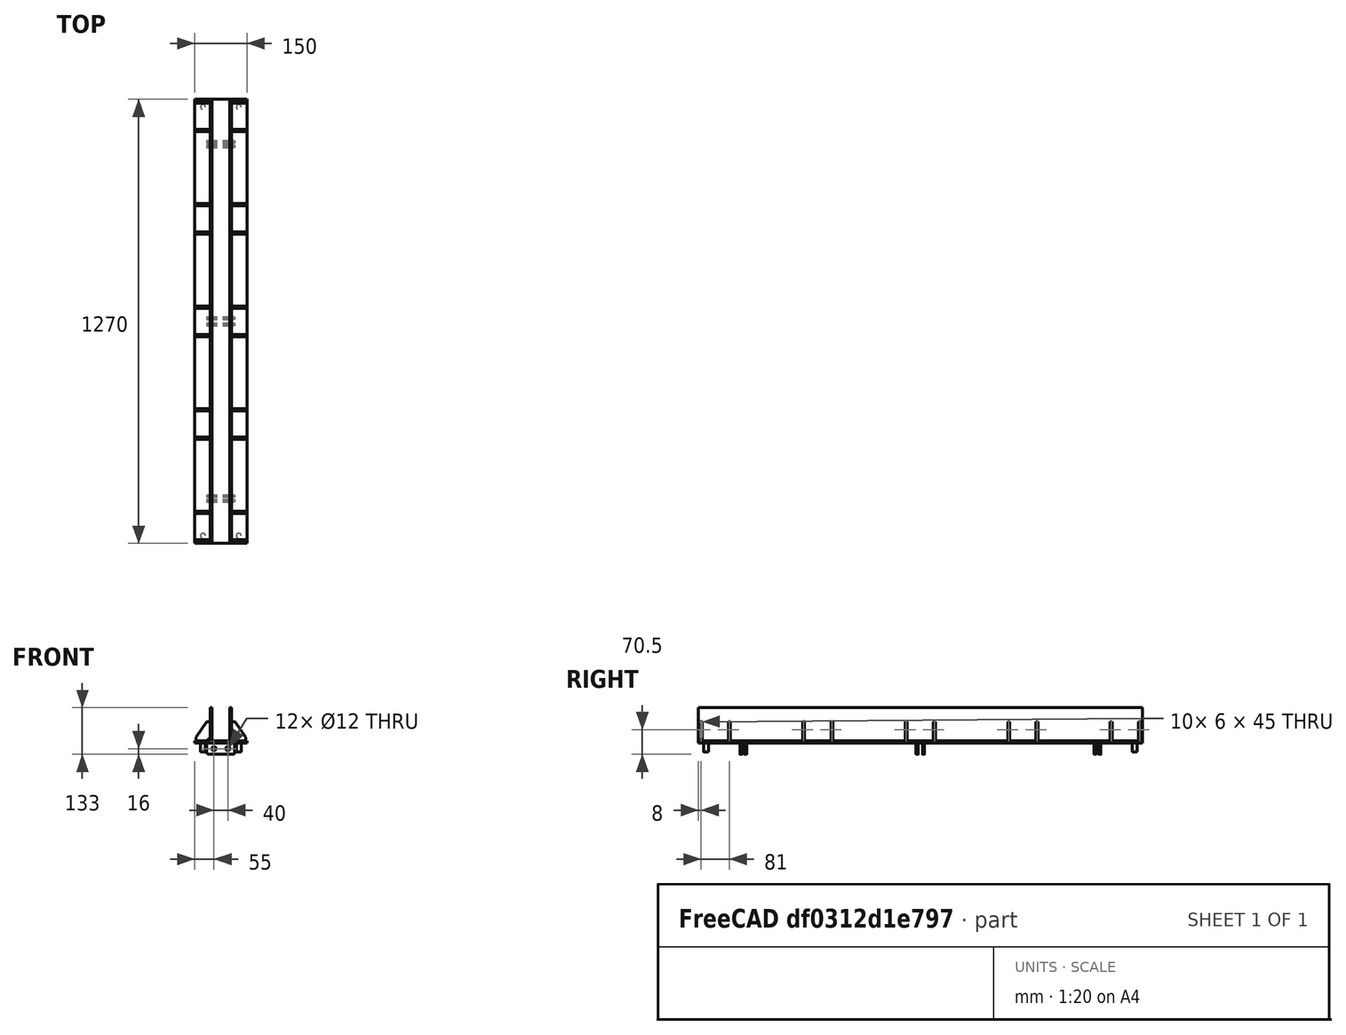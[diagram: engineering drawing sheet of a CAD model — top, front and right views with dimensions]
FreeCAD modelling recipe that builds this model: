
FCSTD DOCUMENT  (FreeCAD 0.21R33771 (Git))
Label: Transom 1270_95_10kN_half
License: All rights reserved
LicenseURL: https://en.wikipedia.org/wiki/All_rights_reserved
objects: Part::FeaturePython×12, Sketcher::SketchObject×3, Fem::ConstraintDisplacement×2, PartDesign::Pad×1, PartDesign::Body×1, Part::Cylinder×1, Part::Compound×1, App::MaterialObjectPython×1, Fem::FemSolverObjectPython×1, Part::MultiFuse×1, Fem::ConstraintForce×1, Fem::FemMeshObjectPython×1, Fem::FemAnalysis×1
note: 19 computed .brp shape members not serialized (recipe doc carries the construction recipe); baked Part::Feature solids carry a one-line shape summary decoded from their .brp

FEATURE [Sketcher::SketchObject] Sketch
  FullyConstrained = true
  MapMode = 5
  Placement = pos=(0,0,0) rot=(1,0,0;1.5708rad)
  sketch-geometry (14):
    g0: LineSegment StartX=0 StartY=0 StartZ=0 EndX=75 EndY=0 EndZ=0
    g1: LineSegment StartX=75 StartY=0 StartZ=0 EndX=75 EndY=6 EndZ=0
    g2: LineSegment StartX=75 StartY=6 StartZ=0 EndX=31 EndY=6 EndZ=0
    g3: LineSegment StartX=31 StartY=6 StartZ=0 EndX=31 EndY=101 EndZ=0
    g4: LineSegment StartX=31 StartY=101 StartZ=0 EndX=25 EndY=101 EndZ=0
    g5: LineSegment StartX=25 StartY=101 StartZ=0 EndX=25 EndY=6 EndZ=0
    g6: LineSegment StartX=25 StartY=6 StartZ=0 EndX=0 EndY=6 EndZ=0
    g7: LineSegment StartX=0 StartY=6 StartZ=0 EndX=-25 EndY=6 EndZ=0
    g8: LineSegment StartX=-25 StartY=6 StartZ=0 EndX=-25 EndY=101 EndZ=0
    g9: LineSegment StartX=-25 StartY=101 StartZ=0 EndX=-31 EndY=101 EndZ=0
    g10: LineSegment StartX=-31 StartY=101 StartZ=0 EndX=-31 EndY=6 EndZ=0
    g11: LineSegment StartX=-31 StartY=6 StartZ=0 EndX=-75 EndY=6 EndZ=0
    g12: LineSegment StartX=-75 StartY=6 StartZ=0 EndX=-75 EndY=0 EndZ=0
    g13: LineSegment StartX=-75 StartY=0 StartZ=0 EndX=0 EndY=0 EndZ=0
  constraints (41):
    c: Coincident(g-1,g0)
    c: PointOnObject(g0,g-1)
    c: Coincident(g0,g1)
    c: Coincident(g1,g2)
    c: Horizontal(g2)
    c: Coincident(g2,g3)
    c: Vertical(g3)
    c: Coincident(g3,g4)
    c: Horizontal(g4)
    c: Coincident(g4,g5)
    c: Vertical(g5)
    c: Coincident(g5,g6)
    c: PointOnObject(g6,g-2)
    c: Horizontal(g6)
    c: DistanceX(g4,g4) = 6
    c: Vertical(g1)
    c: DistanceY(g1,g1) = 6
    c: DistanceY(g0,g6) = 6
    c: DistanceX(g6,g5) = 25
    c: DistanceX(g0,g0) = 75
    c: DistanceY(g3,g3) = 95
    c: Coincident(g6,g7)
    c: Coincident(g7,g8)
    c: Vertical(g8)
    c: Coincident(g8,g9)
    c: Horizontal(g9)
    c: Coincident(g9,g10)
    c: Vertical(g10)
    c: Coincident(g10,g11)
    c: Horizontal(g11)
    c: Coincident(g11,g12)
    c: Coincident(g12,g13)
    c: Coincident(g13,g-1)
    c: Horizontal(g13)
    c: Equal(g5,g10)
    c: Horizontal(g4,g8)
    c: Horizontal(g5,g7)
    c: Vertical(g12)
    c: Equal(g6,g7)
    c: Equal(g2,g11)
    c: Equal(g4,g9)
FEATURE [PartDesign::Pad] Pad
  Direction = (0,-1,2e-16)
  Length = 1270
  Length2 = 10
  Placement = pos=(0,0,0) rot=(1,0,0;1.5708rad)
  Profile = -> Sketch
  ReferenceAxis = -> Sketch [N_Axis]
  Refine = true
  Type = 0
FEATURE [PartDesign::Body] Body
  Group = -> [Sketch,Pad]
  Origin = -> Origin
  Placement = pos=(0,0,0) rot=(0,0,1;3.14159rad)
  Tip = -> Pad
FEATURE [Part::Cylinder] Cylinder
  Angle = 360
  AttacherType = Attacher::AttachEngine3D
  FirstAngle = 0
  Height = 25
  Placement = pos=(51,22,0) rot=(1,0,0;3.14159rad)
  Radius = 7
  SecondAngle = 0
FEATURE [Part::FeaturePython] Array  label="Array_ Transom to Jack Pin"  # Draft array (typed FeaturePython)
  AlwaysSyncPlacement = false
  Angle = 360
  ArrayType = 0
  Axis = (0,0,1)
  Base = -> Cylinder
  Center = (0,0,0)
  Count = 4
  ExpandArray = false
  Fuse = false
  IntervalAxis = (0,0,0)
  IntervalX = (-102,0,0)
  IntervalY = (0,1226,0)
  IntervalZ = (0,0,100)
  NumberCircles = 3
  NumberPolar = 5
  NumberX = 2
  NumberY = 2
  NumberZ = 1
  PlacementList = 4 placements: [(51,22,0),(51,1248,0),(-51,22,0),(-51,1248,0)]
  RadialDistance = 50
  ScaleList = (4) [(1,1,1),(1,1,1),(1,1,1),(1,1,1)]
  Symmetry = 1
  TangentialDistance = 25
FEATURE [Part::FeaturePython] b_Transom_Web_001_  label="Transom Web_Body_001"  # a2plus imported part (geometry in sourceFile) (typed FeaturePython)
  Placement = pos=(31,11,6) rot=(0,0,1;0rad)
  a2p_Version = 0.4.68
  fixedPosition = true
  objectType = a2pPart
  sourceFile = ./Transom Web.FCStd
  sourcePart = Body
  subassemblyImport = false
  timeLastImport = 1.75005e+09
  updateColors = true
FEATURE [Part::FeaturePython] b_Transom_Cleat_001_  label="Transom Cleat_001"  # a2plus imported part (geometry in sourceFile) (typed FeaturePython)
  Placement = pos=(0,125,0) rot=(0,0,1;0rad)
  a2p_Version = 0.4.68
  fixedPosition = true
  objectType = a2pPart
  sourceFile = ./Transom Cleat.FCStd
  subassemblyImport = false
  timeLastImport = 1.75161e+09
  updateColors = true
FEATURE [Part::FeaturePython] b_Transom_Cleat_001_001  label="Transom Cleat_002"  # a2plus imported part (geometry in sourceFile) (typed FeaturePython)
  Placement = pos=(0,138,0) rot=(0,0,1;0rad)
  a2p_Version = 0.4.68
  fixedPosition = false
  objectType = a2pPart
  sourceFile = ./Transom Cleat.FCStd
  subassemblyImport = false
  timeLastImport = 1.75161e+09
  updateColors = true
FEATURE [Part::FeaturePython] b_Transom_Cleat_001_002  label="Transom Cleat_003"  # a2plus imported part (geometry in sourceFile) (typed FeaturePython)
  Placement = pos=(0,1138,0) rot=(0,0,1;0rad)
  a2p_Version = 0.4.68
  fixedPosition = false
  objectType = a2pPart
  sourceFile = ./Transom Cleat.FCStd
  subassemblyImport = false
  timeLastImport = 1.75161e+09
  updateColors = true
FEATURE [Part::FeaturePython] b_Transom_Cleat_001_003  label="Transom Cleat_004"  # a2plus imported part (geometry in sourceFile) (typed FeaturePython)
  Placement = pos=(0,1151,0) rot=(0,0,1;0rad)
  a2p_Version = 0.4.68
  fixedPosition = false
  objectType = a2pPart
  sourceFile = ./Transom Cleat.FCStd
  subassemblyImport = false
  timeLastImport = 1.75161e+09
  updateColors = true
FEATURE [Sketcher::SketchObject] Sketch001
  FullyConstrained = true
  Placement = pos=(0,0,6) rot=(0,0,1;0rad)
  sketch-geometry (40):
    g0: LineSegment StartX=31 StartY=81 StartZ=0 EndX=31 EndY=16 EndZ=0
    g1: LineSegment StartX=31 StartY=16 StartZ=0 EndX=81 EndY=16 EndZ=0
    g2: LineSegment StartX=81 StartY=16 StartZ=0 EndX=81 EndY=81 EndZ=0
    g3: LineSegment StartX=81 StartY=81 StartZ=0 EndX=31 EndY=81 EndZ=0
    g4: LineSegment StartX=31 StartY=667.5 StartZ=0 EndX=31 EndY=602.5 EndZ=0
    g5: LineSegment StartX=31 StartY=602.5 StartZ=0 EndX=81 EndY=602.5 EndZ=0
    g6: LineSegment StartX=81 StartY=602.5 StartZ=0 EndX=81 EndY=667.5 EndZ=0
    g7: LineSegment StartX=81 StartY=667.5 StartZ=0 EndX=31 EndY=667.5 EndZ=0
    g8: LineSegment StartX=31 StartY=1189 StartZ=0 EndX=31 EndY=1254 EndZ=0
    g9: LineSegment StartX=31 StartY=1254 StartZ=0 EndX=81 EndY=1254 EndZ=0
    g10: LineSegment StartX=81 StartY=1254 StartZ=0 EndX=81 EndY=1189 EndZ=0
    g11: LineSegment StartX=81 StartY=1189 StartZ=0 EndX=31 EndY=1189 EndZ=0
    g12: LineSegment StartX=31 StartY=374.25 StartZ=0 EndX=31 EndY=309.25 EndZ=0
    g13: LineSegment StartX=31 StartY=309.25 StartZ=0 EndX=81 EndY=309.25 EndZ=0
    g14: LineSegment StartX=81 StartY=309.25 StartZ=0 EndX=81 EndY=374.25 EndZ=0
    g15: LineSegment StartX=81 StartY=374.25 StartZ=0 EndX=31 EndY=374.25 EndZ=0
    g16: LineSegment StartX=31 StartY=960.75 StartZ=0 EndX=31 EndY=895.75 EndZ=0
    g17: LineSegment StartX=31 StartY=895.75 StartZ=0 EndX=81 EndY=895.75 EndZ=0
    g18: LineSegment StartX=81 StartY=895.75 StartZ=0 EndX=81 EndY=960.75 EndZ=0
    g19: LineSegment StartX=81 StartY=960.75 StartZ=0 EndX=31 EndY=960.75 EndZ=0
    g20: LineSegment StartX=-31 StartY=81 StartZ=0 EndX=-31 EndY=16 EndZ=0
    g21: LineSegment StartX=-31 StartY=16 StartZ=0 EndX=-81 EndY=16 EndZ=0
    g22: LineSegment StartX=-81 StartY=16 StartZ=0 EndX=-81 EndY=81 EndZ=0
    g23: LineSegment StartX=-81 StartY=81 StartZ=0 EndX=-31 EndY=81 EndZ=0
    g24: LineSegment StartX=-31 StartY=667.5 StartZ=0 EndX=-31 EndY=602.5 EndZ=0
    g25: LineSegment StartX=-31 StartY=602.5 StartZ=0 EndX=-81 EndY=602.5 EndZ=0
    g26: LineSegment StartX=-81 StartY=602.5 StartZ=0 EndX=-81 EndY=667.5 EndZ=0
    g27: LineSegment StartX=-81 StartY=667.5 StartZ=0 EndX=-31 EndY=667.5 EndZ=0
    g28: LineSegment StartX=-31 StartY=1189 StartZ=0 EndX=-31 EndY=1254 EndZ=0
    g29: LineSegment StartX=-31 StartY=1254 StartZ=0 EndX=-81 EndY=1254 EndZ=0
    g30: LineSegment StartX=-81 StartY=1254 StartZ=0 EndX=-81 EndY=1189 EndZ=0
    g31: LineSegment StartX=-81 StartY=1189 StartZ=0 EndX=-31 EndY=1189 EndZ=0
    g32: LineSegment StartX=-31 StartY=374.25 StartZ=0 EndX=-31 EndY=309.25 EndZ=0
    g33: LineSegment StartX=-31 StartY=309.25 StartZ=0 EndX=-81 EndY=309.25 EndZ=0
    g34: LineSegment StartX=-81 StartY=309.25 StartZ=0 EndX=-81 EndY=374.25 EndZ=0
    g35: LineSegment StartX=-81 StartY=374.25 StartZ=0 EndX=-31 EndY=374.25 EndZ=0
    g36: LineSegment StartX=-31 StartY=960.75 StartZ=0 EndX=-31 EndY=895.75 EndZ=0
    g37: LineSegment StartX=-31 StartY=895.75 StartZ=0 EndX=-81 EndY=895.75 EndZ=0
    g38: LineSegment StartX=-81 StartY=895.75 StartZ=0 EndX=-81 EndY=960.75 EndZ=0
    g39: LineSegment StartX=-81 StartY=960.75 StartZ=0 EndX=-31 EndY=960.75 EndZ=0
  constraints (120):
    c: Coincident(g0,g1)
    c: Coincident(g1,g2)
    c: Coincident(g2,g3)
    c: Coincident(g3,g0)
    c: Vertical(g0)
    c: Vertical(g2)
    c: Horizontal(g1)
    c: Horizontal(g3)
    c: DistanceY(g2,g2) = 65
    c: DistanceX(g3,g3) = 50
    c: DistanceY(g-1,g0) = 16
    c: DistanceX(g-1,g0) = 31
    c: Coincident(g4,g5)
    c: Coincident(g5,g6)
    c: Coincident(g6,g7)
    c: Coincident(g7,g4)
    c: Vertical(g4)
    c: Vertical(g6)
    c: Horizontal(g5)
    c: Horizontal(g7)
    c: Coincident(g8,g9)
    c: Coincident(g9,g10)
    c: Coincident(g10,g11)
    c: Coincident(g11,g8)
    c: Vertical(g8)
    c: Vertical(g10)
    c: Horizontal(g9)
    c: Horizontal(g11)
    c: Equal(g2,g6)
    c: Equal(g6,g10)
    c: Equal(g1,g5)
    c: Equal(g5,g9)
    c: Vertical(g2,g6)
    c: Vertical(g6,g10)
    c: DistanceY(g2,g5) = 521.5
    c: DistanceY(g6,g9) = 586.5
    c: Coincident(g12,g13)
    c: Coincident(g13,g14)
    c: Coincident(g14,g15)
    c: Coincident(g15,g12)
    c: Vertical(g12)
    c: Vertical(g14)
    c: Horizontal(g13)
    c: Horizontal(g15)
    c: Coincident(g16,g17)
    c: Coincident(g17,g18)
    c: Coincident(g18,g19)
    c: Coincident(g19,g16)
    c: Vertical(g16)
    c: Vertical(g18)
    c: Horizontal(g17)
    c: Horizontal(g19)
    c: Vertical(g0,g12)
    c: Vertical(g12,g16)
    c: Vertical(g2,g13)
    c: Vertical(g13,g17)
    c: Equal(g0,g12)
    c: Equal(g12,g16)
    c: DistanceY(g2,g13) = 228.25
    c: DistanceY(g6,g17) = 228.25
    c: Coincident(g20,g21)
    c: Coincident(g21,g22)
    c: Coincident(g22,g23)
    c: Coincident(g23,g20)
    c: Vertical(g20)
    c: Vertical(g22)
    c: Horizontal(g21)
    c: Horizontal(g23)
    c: Coincident(g24,g25)
    c: Coincident(g25,g26)
    c: Coincident(g26,g27)
    c: Coincident(g27,g24)
    c: Vertical(g24)
    c: Vertical(g26)
    c: Horizontal(g25)
    c: Horizontal(g27)
    c: Coincident(g28,g29)
    c: Coincident(g29,g30)
    c: Coincident(g30,g31)
    c: Coincident(g31,g28)
    c: Vertical(g28)
    c: Vertical(g30)
    c: Horizontal(g29)
    c: Horizontal(g31)
    c: Equal(g22,g26)
    c: Equal(g26,g30)
    c: Equal(g21,g25)
    c: Equal(g25,g29)
    c: Coincident(g32,g33)
    c: Coincident(g33,g34)
    c: Coincident(g34,g35)
    c: Coincident(g35,g32)
    c: Vertical(g32)
    c: Vertical(g34)
    c: Horizontal(g33)
    c: Horizontal(g35)
    c: Coincident(g36,g37)
    c: Coincident(g37,g38)
    c: Coincident(g38,g39)
    c: Coincident(g39,g36)
    c: Vertical(g36)
    c: Vertical(g38)
    c: Horizontal(g37)
    c: Horizontal(g39)
    c: Equal(g20,g32)
    c: Equal(g32,g36)
    c: Horizontal(g32,g12)
    c: Horizontal(g24,g4)
    c: Horizontal(g36,g16)
    c: Horizontal(g28,g8)
    c: Vertical(g21,g33)
    c: Vertical(g33,g25)
    c: Vertical(g25,g37)
    c: Vertical(g37,g30)
    c: Equal(g0,g22)
    c: DistanceY(g-1,g20) = 16
    c: DistanceX(g20,g-1) = 31
    c: Equal(g3,g23)
    c: Equal(g15,g35)
    c: Equal(g19,g39)
FEATURE [Part::FeaturePython] b_Transom_Cleat_001_004  label="Transom Cleat_005"  # a2plus imported part (geometry in sourceFile) (typed FeaturePython)
  Placement = pos=(0,647,0) rot=(0,0,1;0rad)
  a2p_Version = 0.4.68
  fixedPosition = false
  objectType = a2pPart
  sourceFile = ./Transom Cleat.FCStd
  subassemblyImport = false
  timeLastImport = 1.75161e+09
  updateColors = true
FEATURE [Part::FeaturePython] b_Transom_Cleat_001_005  label="Transom Cleat_006"  # a2plus imported part (geometry in sourceFile) (typed FeaturePython)
  Placement = pos=(-4.61864e-06,629,3.05661e-08) rot=(0,0,1;0rad)
  a2p_Version = 0.4.68
  fixedPosition = false
  objectType = a2pPart
  sourceFile = ./Transom Cleat.FCStd
  subassemblyImport = false
  timeLastImport = 1.75161e+09
  updateColors = true
FEATURE [Sketcher::SketchObject] Sketch002
  FullyConstrained = true
  MapMode = 5
  Placement = pos=(0,0,1e-15) rot=(1,0,0;3.14159rad)
  sketch-geometry (12):
    g0: LineSegment StartX=-80 StartY=-55 StartZ=0 EndX=-80 EndY=-75 EndZ=0
    g1: LineSegment StartX=-80 StartY=-75 StartZ=0 EndX=80 EndY=-75 EndZ=0
    g2: LineSegment StartX=80 StartY=-75 StartZ=0 EndX=80 EndY=-55 EndZ=0
    g3: LineSegment StartX=80 StartY=-55 StartZ=0 EndX=-80 EndY=-55 EndZ=0
    g4: LineSegment StartX=-80 StartY=-1195 StartZ=0 EndX=-80 EndY=-1215 EndZ=0
    g5: LineSegment StartX=-80 StartY=-1215 StartZ=0 EndX=80 EndY=-1215 EndZ=0
    g6: LineSegment StartX=80 StartY=-1215 StartZ=0 EndX=80 EndY=-1195 EndZ=0
    g7: LineSegment StartX=80 StartY=-1195 StartZ=0 EndX=-80 EndY=-1195 EndZ=0
    g8: LineSegment StartX=-80 StartY=-629 StartZ=0 EndX=-80 EndY=-641 EndZ=0
    g9: LineSegment StartX=-80 StartY=-641 StartZ=0 EndX=80 EndY=-641 EndZ=0
    g10: LineSegment StartX=80 StartY=-641 StartZ=0 EndX=80 EndY=-629 EndZ=0
    g11: LineSegment StartX=80 StartY=-629 StartZ=0 EndX=-80 EndY=-629 EndZ=0
  constraints (33):
    c: Coincident(g0,g1)
    c: Coincident(g1,g2)
    c: Coincident(g2,g3)
    c: Coincident(g3,g0)
    c: Vertical(g0)
    c: Vertical(g2)
    c: Horizontal(g3)
    c: Distance(g0,g2) = 160
    c: Distance(g1,g3) = 20
    c: Coincident(g4,g5)
    c: Coincident(g5,g6)
    c: Coincident(g6,g7)
    c: Coincident(g7,g4)
    c: Vertical(g4)
    c: Vertical(g6)
    c: Horizontal(g7)
    c: Symmetric(g0,g1,g-2)
    c: DistanceY(g1,g-1) = 75
    c: Equal(g3,g7)
    c: Symmetric(g4,g5,g-2)
    c: DistanceY(g6,g6) = 20
    c: DistanceY(g6,g-1) = 1195
    c: Coincident(g8,g9)
    c: Coincident(g9,g10)
    c: Coincident(g10,g11)
    c: Coincident(g11,g8)
    c: Vertical(g8)
    c: Vertical(g10)
    c: Horizontal(g11)
    c: DistanceY(g10,g10) = 12
    c: DistanceX(g9,g9) = 160
    c: Symmetric(g8,g9,g-2)
    c: DistanceY(g10,g-1) = 629
FEATURE [Part::FeaturePython] b_Transom_Web_Body_001_  label="Transom Web_Body_002"  # a2plus imported part (geometry in sourceFile) (typed FeaturePython)
  Placement = pos=(31,92,6) rot=(0,0,1;0rad)
  a2p_Version = 0.4.68
  fixedPosition = false
  objectType = a2pPart
  sourceFile = ./Transom Web.FCStd
  sourcePart = Body
  subassemblyImport = false
  timeLastImport = 1.75005e+09
  updateColors = true
FEATURE [Part::FeaturePython] b_Transom_Web_Body_001_001  label="Transom Web_Body_003"  # a2plus imported part (geometry in sourceFile) (typed FeaturePython)
  Placement = pos=(-31,5,6) rot=(0,0,1;3.14159rad)
  a2p_Version = 0.4.68
  fixedPosition = false
  objectType = a2pPart
  sourceFile = ./Transom Web.FCStd
  sourcePart = Body
  subassemblyImport = false
  timeLastImport = 1.75005e+09
  updateColors = true
FEATURE [Part::FeaturePython] b_Transom_Web_Body_001_002  label="Transom Web_Body_004"  # a2plus imported part (geometry in sourceFile) (typed FeaturePython)
  Placement = pos=(-31,86,6) rot=(0,0,1;3.14159rad)
  a2p_Version = 0.4.68
  fixedPosition = false
  objectType = a2pPart
  sourceFile = ./Transom Web.FCStd
  sourcePart = Body
  subassemblyImport = false
  timeLastImport = 1.75005e+09
  updateColors = true
FEATURE [Part::Compound] Compound  label="Compound of Webs"
  Links = -> [b_Transom_Web_001_,b_Transom_Web_Body_001_,b_Transom_Web_Body_001_001,b_Transom_Web_Body_001_002]
FEATURE [Part::FeaturePython] Array001  label="Array of Webs"  # Draft array (typed FeaturePython)
  AlwaysSyncPlacement = false
  Angle = 360
  ArrayType = 0
  Axis = (0,0,1)
  Base = -> Compound
  Center = (0,0,0)
  Count = 5
  ExpandArray = false
  Fuse = false
  IntervalAxis = (0,0,0)
  IntervalX = (1270,0,0)
  IntervalY = (0,293.25,0)
  IntervalZ = (0,0,100)
  NumberCircles = 3
  NumberPolar = 5
  NumberX = 1
  NumberY = 5
  NumberZ = 1
  PlacementList = 5 placements: arithmetic series from (0,0,0) step (0,293.25,0) to (0,1173,0)
  RadialDistance = 50
  ScaleList = (5) [(1,1,1),(1,1,1),(1,1,1),(1,1,1),(1,1,1)]
  Symmetry = 1
  TangentialDistance = 25
FEATURE [App::MaterialObjectPython] MaterialSolid  label="steel"  # material (typed FeaturePython)
  Category = 0
  Material = AmbientColor=(0.0020, 0.0020, 0.0020, 1.0),Author=M. Münch,AuthorAndLicense=LGPL-2.0-or-later,CardName=Steel-S235JO,Density=7.8e-06 kg/mm^3,+18 more (map truncated)
  UUID = 5b13e02a-b173-4e2d-95fd-a30d9e0f7cf5
FEATURE [Fem::FemSolverObjectPython] SolverCcxTools  # FEM object (typed FeaturePython)
  AnalysisType = 4
  BeamReducedIntegration = true
  BeamShellResultOutput3D = true
  BucklingFactors = 5
  EigenmodeHighLimit = 1000000
  EigenmodeLowLimit = 0
  EigenmodesCount = 10
  GeometricalNonlinearity = 0
  IterationsControlParameterCutb = 0.25,0.5,0.75,0.85,,,1.5,
  IterationsControlParameterIter = 4,8,9,200,10,400,,200,,
  IterationsControlParameterTimeUse = false
  IterationsMaximum = 2000
  IterationsThermoMechMaximum = 2000
  IterationsUserDefinedIncrementations = false
  IterationsUserDefinedTimeStepLength = false
  MaterialNonlinearity = 0
  MatrixSolverType = 0
  ModelSpace = 0
  OutputFrequency = 1
  SplitInputWriter = true
  ThermoMechSteadyState = true
  ThermoMechType = 0
  TimeEnd = 1
  TimeInitialStep = 0.01
  TimeMaximumStep = 1
  TimeMinimumStep = 1e-05
FEATURE [Part::MultiFuse] Fusion
  Refine = true
  Shapes = -> [Body,Array,Array001,b_Transom_Cleat_001_,b_Transom_Cleat_001_001,b_Transom_Cleat_001_002,b_Transom_Cleat_001_003,b_Transom_Cleat_001_004,b_Transom_Cleat_001_005]
FEATURE [Fem::ConstraintDisplacement] ConstraintDisplacement  label="XYZ"
  NormalDirection = (0,2e-16,-1)
  Normals = (4) [(0,2e-16,-1),(0,2e-16,-1),(0,2e-16,-1),(0,2e-16,-1)]
  Points = (4) [(75,0,0),(25,0,0),(-25,0,0),(-75,0,0)]
  References = -> [Fusion]
  Scale = 13
  hasXFormula = false
  hasYFormula = false
  hasZFormula = false
  rotxFix = false
  rotxFree = true
  rotyFix = false
  rotyFree = true
  rotzFix = false
  rotzFree = true
  useFlowSurfaceForce = false
  xDisplacement = 0
  xFix = false
  xFree = false
  xRotation = 0
  yDisplacement = 0
  yFix = false
  yFree = false
  yRotation = 0
  zDisplacement = 0
  zFix = false
  zFree = false
  zRotation = 0
FEATURE [Fem::ConstraintDisplacement] ConstraintDisplacement001  label="XZ"
  NormalDirection = (0,2e-16,-1)
  Normals = (4) [(0,2e-16,-1),(0,2e-16,-1),(0,2e-16,-1),(0,2e-16,-1)]
  Points = (4) [(75,1270,2.82e-13),(25,1270,2.82e-13),(-25,1270,2.82e-13),(-75,1270,2.82e-13)]
  References = -> [Fusion]
  Scale = 13
  hasXFormula = false
  hasYFormula = false
  hasZFormula = false
  rotxFix = false
  rotxFree = true
  rotyFix = false
  rotyFree = true
  rotzFix = false
  rotzFree = true
  useFlowSurfaceForce = false
  xDisplacement = 0
  xFix = false
  xFree = false
  xRotation = 0
  yDisplacement = 0
  yFix = false
  yFree = true
  yRotation = 0
  zDisplacement = 0
  zFix = false
  zFree = false
  zRotation = 0
FEATURE [Fem::ConstraintForce] ConstraintForce  label="100kN"
  DirectionVector = (0,2e-16,-1)
  Force = 100000
  NormalDirection = (0,-2e-16,1)
  Points = (24) [(31,1270,6),(45.6667,1270,6),(60.3333,1270,6),(75,1270,6),(31,1016,6),(45.6667,1016,6),(60.3333,1016,6),(75,1016,6),(31,762,6),(45.6667,762,6),+14 more]
  References = -> [Fusion]
  Reversed = true
  Scale = 27
FEATURE [Fem::FemMeshObjectPython] FEMMeshGmsh  # FEM object (typed FeaturePython)
  Algorithm2D = 0
  Algorithm3D = 0
  CharacteristicLengthMax = 6
  CharacteristicLengthMin = 0
  CoherenceMesh = true
  ElementDimension = 0
  ElementOrder = 1
  GeometryTolerance = 1e-06
  GroupsOfNodes = false
  HighOrderOptimize = 0
  MeshSizeFromCurvature = 12
  OptimizeNetgen = false
  OptimizeStd = true
  Part = -> Fusion
  RecombinationAlgorithm = 0
  Recombine3DAll = false
  RecombineAll = false
  SecondOrderLinear = false
FEATURE [Fem::FemAnalysis] Analysis
  Group = -> [MaterialSolid,ConstraintDisplacement,ConstraintDisplacement001,ConstraintForce,SolverCcxTools,FEMMeshGmsh]
